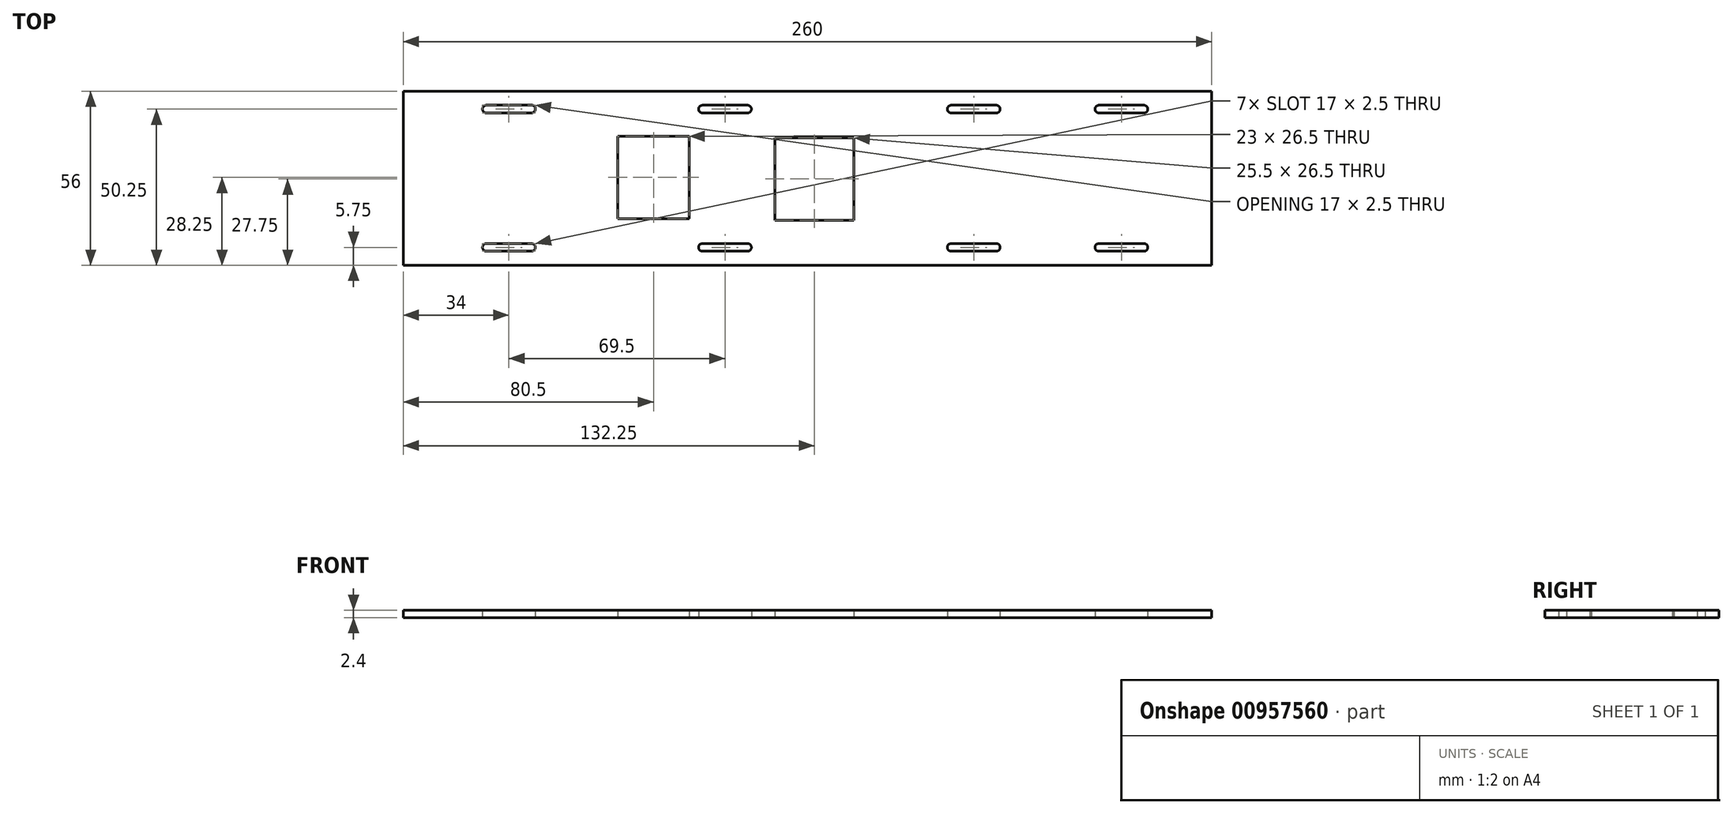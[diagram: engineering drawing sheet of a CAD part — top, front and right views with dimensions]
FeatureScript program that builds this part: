
annotation { "Feature Type Name" : "Feature", "Feature Type Description" : "" }
export const myFeature = defineFeature(function(context is Context, id is Id, definition is map)
    precondition{}
    {
        {
            var Q0;
            Q0=qCreatedBy(makeId("Top.planeOp"),FACE);
            var sketch = newSketch(context, id + "F0", { "sketchPlane" : qUnion([Q0])});
            skLineSegment(sketch, "E0.bottom", {"start": v(130, -28) * mm, "end": v(-130, -28) * mm});
            skLineSegment(sketch, "E0.top", {"start": v(130, 28) * mm, "end": v(-130, 28) * mm});
            skLineSegment(sketch, "E0.left", {"start": v(130, -28) * mm, "end": v(130, 28) * mm});
            skLineSegment(sketch, "E0.right", {"start": v(-130, -28) * mm, "end": v(-130, 28) * mm});
            skPoint(sketch, "E0.middle", {"position": v(0, 0) * mm});
            skLineSegment(sketch, "E1", {"start": v(-130, 28) * mm, "end": v(-104.5, 28) * mm});
            skLineSegment(sketch, "E2", {"start": v(-103.25, 23.5) * mm, "end": v(-88.5, 23.5) * mm});
            skLineSegment(sketch, "E3", {"start": v(-87.5, 22.5) * mm, "end": v(-87.5, 22.25) * mm});
            skLineSegment(sketch, "E4", {"start": v(-88.75, 21) * mm, "end": v(-103.25, 21) * mm});
            skLineSegment(sketch, "E5", {"start": v(-104.5, 22.25) * mm, "end": v(-104.5, 22.25) * mm});
            skLineSegment(sketch, "E6", {"start": v(-130, -28) * mm, "end": v(-104.5, -28) * mm});
            skLineSegment(sketch, "E7.bottom", {"start": v(-103.25, -23.5) * mm, "end": v(-88.75, -23.5) * mm});
            skLineSegment(sketch, "E7.top", {"start": v(-103.25, -21) * mm, "end": v(-88.75, -21) * mm});
            skLineSegment(sketch, "E7.left", {"start": v(-104.5, -22.25) * mm, "end": v(-104.5, -22.25) * mm});
            skLineSegment(sketch, "E7.right", {"start": v(-87.5, -22.25) * mm, "end": v(-87.5, -22.25) * mm});
            skLineSegment(sketch, "E8", {"start": v(-130, -28) * mm, "end": v(-35, -28) * mm});
            skLineSegment(sketch, "E9.bottom", {"start": v(-33.75, -23.5) * mm, "end": v(-19.25, -23.5) * mm});
            skLineSegment(sketch, "E9.top", {"start": v(-33.75, -21) * mm, "end": v(-19.25, -21) * mm});
            skLineSegment(sketch, "E9.left", {"start": v(-35, -22.25) * mm, "end": v(-35, -22.25) * mm});
            skLineSegment(sketch, "E9.right", {"start": v(-18, -22.25) * mm, "end": v(-18, -22.25) * mm});
            skLineSegment(sketch, "E10", {"start": v(-130, 28) * mm, "end": v(-35, 28) * mm});
            skLineSegment(sketch, "E11.bottom", {"start": v(-33.75, 23.5) * mm, "end": v(-19.25, 23.5) * mm});
            skLineSegment(sketch, "E11.top", {"start": v(-33.75, 21) * mm, "end": v(-19.25, 21) * mm});
            skLineSegment(sketch, "E11.left", {"start": v(-35, 22.25) * mm, "end": v(-35, 22.25) * mm});
            skLineSegment(sketch, "E11.right", {"start": v(-18, 22.25) * mm, "end": v(-18, 22.25) * mm});
            skLineSegment(sketch, "E12", {"start": v(130, 28) * mm, "end": v(109.5, 28) * mm});
            skLineSegment(sketch, "E13.bottom", {"start": v(108.25, 23.5) * mm, "end": v(93.75, 23.5) * mm});
            skLineSegment(sketch, "E13.top", {"start": v(108.25, 21) * mm, "end": v(93.75, 21) * mm});
            skLineSegment(sketch, "E13.left", {"start": v(109.5, 22.25) * mm, "end": v(109.5, 22.25) * mm});
            skLineSegment(sketch, "E13.right", {"start": v(92.5, 22.25) * mm, "end": v(92.5, 22.25) * mm});
            skLineSegment(sketch, "E14.bottom", {"start": v(60.75, 23.5) * mm, "end": v(46.25, 23.5) * mm});
            skLineSegment(sketch, "E14.top", {"start": v(60.75, 21) * mm, "end": v(46.25, 21) * mm});
            skLineSegment(sketch, "E14.left", {"start": v(62, 22.25) * mm, "end": v(62, 22.25) * mm});
            skLineSegment(sketch, "E14.right", {"start": v(45, 22.25) * mm, "end": v(45, 22.25) * mm});
            skLineSegment(sketch, "E15", {"start": v(130, -28) * mm, "end": v(109.5, -28) * mm});
            skLineSegment(sketch, "E16.bottom", {"start": v(108.25, -23.5) * mm, "end": v(93.75, -23.5) * mm});
            skLineSegment(sketch, "E16.top", {"start": v(108.25, -21) * mm, "end": v(93.75, -21) * mm});
            skLineSegment(sketch, "E16.left", {"start": v(109.5, -22.25) * mm, "end": v(109.5, -22.25) * mm});
            skLineSegment(sketch, "E16.right", {"start": v(92.5, -22.25) * mm, "end": v(92.5, -22.25) * mm});
            skLineSegment(sketch, "E17", {"start": v(130, -28) * mm, "end": v(62, -28) * mm});
            skLineSegment(sketch, "E18.bottom", {"start": v(60.75, -23.5) * mm, "end": v(46.25, -23.5) * mm});
            skLineSegment(sketch, "E18.top", {"start": v(60.75, -21) * mm, "end": v(46.25, -21) * mm});
            skLineSegment(sketch, "E18.left", {"start": v(62, -22.25) * mm, "end": v(62, -22.25) * mm});
            skLineSegment(sketch, "E18.right", {"start": v(45, -22.25) * mm, "end": v(45, -22.25) * mm});
            skLineSegment(sketch, "E19", {"start": v(-130, 28) * mm, "end": v(-61, 28) * mm});
            skLineSegment(sketch, "E20", {"start": v(-61, 28) * mm, "end": v(-61, 13.5) * mm});
            skLineSegment(sketch, "E21.bottom", {"start": v(-61, 13.5) * mm, "end": v(-38, 13.5) * mm});
            skLineSegment(sketch, "E21.top", {"start": v(-61, -13) * mm, "end": v(-38, -13) * mm});
            skLineSegment(sketch, "E21.left", {"start": v(-61, 13.5) * mm, "end": v(-61, -13) * mm});
            skLineSegment(sketch, "E21.right", {"start": v(-38, 13.5) * mm, "end": v(-38, -13) * mm});
            skLineSegment(sketch, "E22", {"start": v(-130, -28) * mm, "end": v(-10.5, -28) * mm});
            skLineSegment(sketch, "E23", {"start": v(-10.5, -28) * mm, "end": v(-10.5, -13.5) * mm});
            skLineSegment(sketch, "E24.bottom", {"start": v(-10.5, -13.5) * mm, "end": v(15, -13.5) * mm});
            skLineSegment(sketch, "E24.top", {"start": v(-10.5, 13) * mm, "end": v(15, 13) * mm});
            skLineSegment(sketch, "E24.left", {"start": v(-10.5, -13.5) * mm, "end": v(-10.5, 13) * mm});
            skLineSegment(sketch, "E24.right", {"start": v(15, -13.5) * mm, "end": v(15, 13) * mm});
            skPoint(sketch, "E25.visualSharp", {"position": v(-87.5, 23.5) * mm});
            skArc(sketch, "E25.filletArc", {"start": v(-87.5, 22.5) * mm, "mid": v(-87.8, 23.2) * mm, "end": v(-88.5, 23.5) * mm});
            skPoint(sketch, "E26.visualSharp", {"position": v(-87.5, 21) * mm});
            skArc(sketch, "E26.filletArc", {"start": v(-88.75, 21) * mm, "mid": v(-87.87, 21.37) * mm, "end": v(-87.5, 22.25) * mm});
            skPoint(sketch, "E27.visualSharp", {"position": v(-104.5, 23.5) * mm});
            skArc(sketch, "E27.filletArc", {"start": v(-103.25, 23.5) * mm, "mid": v(-104.13, 23.13) * mm, "end": v(-104.5, 22.25) * mm});
            skPoint(sketch, "E28.visualSharp", {"position": v(-104.5, 21) * mm});
            skArc(sketch, "E28.filletArc", {"start": v(-104.5, 22.25) * mm, "mid": v(-104.13, 21.37) * mm, "end": v(-103.25, 21) * mm});
            skPoint(sketch, "E29.visualSharp", {"position": v(-104.5, -21) * mm});
            skArc(sketch, "E29.filletArc", {"start": v(-103.25, -21) * mm, "mid": v(-104.13, -21.37) * mm, "end": v(-104.5, -22.25) * mm});
            skPoint(sketch, "E30.visualSharp", {"position": v(-104.5, -23.5) * mm});
            skArc(sketch, "E30.filletArc", {"start": v(-104.5, -22.25) * mm, "mid": v(-104.13, -23.13) * mm, "end": v(-103.25, -23.5) * mm});
            skPoint(sketch, "E31.visualSharp", {"position": v(-87.5, -21) * mm});
            skArc(sketch, "E31.filletArc", {"start": v(-87.5, -22.25) * mm, "mid": v(-87.87, -21.37) * mm, "end": v(-88.75, -21) * mm});
            skPoint(sketch, "E32.visualSharp", {"position": v(-87.5, -23.5) * mm});
            skArc(sketch, "E32.filletArc", {"start": v(-88.75, -23.5) * mm, "mid": v(-87.87, -23.13) * mm, "end": v(-87.5, -22.25) * mm});
            skPoint(sketch, "E33.visualSharp", {"position": v(-35, 23.5) * mm});
            skArc(sketch, "E33.filletArc", {"start": v(-33.75, 23.5) * mm, "mid": v(-34.63, 23.13) * mm, "end": v(-35, 22.25) * mm});
            skPoint(sketch, "E34.visualSharp", {"position": v(-35, 21) * mm});
            skArc(sketch, "E34.filletArc", {"start": v(-35, 22.25) * mm, "mid": v(-34.63, 21.37) * mm, "end": v(-33.75, 21) * mm});
            skPoint(sketch, "E35.visualSharp", {"position": v(-18, 23.5) * mm});
            skArc(sketch, "E35.filletArc", {"start": v(-18, 22.25) * mm, "mid": v(-18.37, 23.13) * mm, "end": v(-19.25, 23.5) * mm});
            skPoint(sketch, "E36.visualSharp", {"position": v(-18, 21) * mm});
            skArc(sketch, "E36.filletArc", {"start": v(-19.25, 21) * mm, "mid": v(-18.37, 21.37) * mm, "end": v(-18, 22.25) * mm});
            skPoint(sketch, "E37.visualSharp", {"position": v(-35, -21) * mm});
            skArc(sketch, "E37.filletArc", {"start": v(-33.75, -21) * mm, "mid": v(-34.63, -21.37) * mm, "end": v(-35, -22.25) * mm});
            skPoint(sketch, "E38.visualSharp", {"position": v(-35, -23.5) * mm});
            skArc(sketch, "E38.filletArc", {"start": v(-35, -22.25) * mm, "mid": v(-34.63, -23.13) * mm, "end": v(-33.75, -23.5) * mm});
            skPoint(sketch, "E39.visualSharp", {"position": v(-18, -21) * mm});
            skArc(sketch, "E39.filletArc", {"start": v(-18, -22.25) * mm, "mid": v(-18.37, -21.37) * mm, "end": v(-19.25, -21) * mm});
            skPoint(sketch, "E40.visualSharp", {"position": v(-18, -23.5) * mm});
            skArc(sketch, "E40.filletArc", {"start": v(-19.25, -23.5) * mm, "mid": v(-18.37, -23.13) * mm, "end": v(-18, -22.25) * mm});
            skPoint(sketch, "E41.visualSharp", {"position": v(45, 23.5) * mm});
            skArc(sketch, "E41.filletArc", {"start": v(46.25, 23.5) * mm, "mid": v(45.37, 23.13) * mm, "end": v(45, 22.25) * mm});
            skPoint(sketch, "E42.visualSharp", {"position": v(45, 21) * mm});
            skArc(sketch, "E42.filletArc", {"start": v(45, 22.25) * mm, "mid": v(45.37, 21.37) * mm, "end": v(46.25, 21) * mm});
            skPoint(sketch, "E43.visualSharp", {"position": v(62, 23.5) * mm});
            skArc(sketch, "E43.filletArc", {"start": v(62, 22.25) * mm, "mid": v(61.63, 23.13) * mm, "end": v(60.75, 23.5) * mm});
            skPoint(sketch, "E44.visualSharp", {"position": v(62, 21) * mm});
            skArc(sketch, "E44.filletArc", {"start": v(60.75, 21) * mm, "mid": v(61.63, 21.37) * mm, "end": v(62, 22.25) * mm});
            skPoint(sketch, "E45.visualSharp", {"position": v(45, -21) * mm});
            skArc(sketch, "E45.filletArc", {"start": v(46.25, -21) * mm, "mid": v(45.37, -21.37) * mm, "end": v(45, -22.25) * mm});
            skPoint(sketch, "E46.visualSharp", {"position": v(45, -23.5) * mm});
            skArc(sketch, "E46.filletArc", {"start": v(45, -22.25) * mm, "mid": v(45.37, -23.13) * mm, "end": v(46.25, -23.5) * mm});
            skPoint(sketch, "E47.visualSharp", {"position": v(62, -21) * mm});
            skArc(sketch, "E47.filletArc", {"start": v(62, -22.25) * mm, "mid": v(61.63, -21.37) * mm, "end": v(60.75, -21) * mm});
            skPoint(sketch, "E48.visualSharp", {"position": v(62, -23.5) * mm});
            skArc(sketch, "E48.filletArc", {"start": v(60.75, -23.5) * mm, "mid": v(61.63, -23.13) * mm, "end": v(62, -22.25) * mm});
            skPoint(sketch, "E49.visualSharp", {"position": v(92.5, 23.5) * mm});
            skArc(sketch, "E49.filletArc", {"start": v(93.75, 23.5) * mm, "mid": v(92.87, 23.13) * mm, "end": v(92.5, 22.25) * mm});
            skPoint(sketch, "E50.visualSharp", {"position": v(92.5, 21) * mm});
            skArc(sketch, "E50.filletArc", {"start": v(92.5, 22.25) * mm, "mid": v(92.87, 21.37) * mm, "end": v(93.75, 21) * mm});
            skPoint(sketch, "E51.visualSharp", {"position": v(109.5, 23.5) * mm});
            skArc(sketch, "E51.filletArc", {"start": v(109.5, 22.25) * mm, "mid": v(109.13, 23.13) * mm, "end": v(108.25, 23.5) * mm});
            skPoint(sketch, "E52.visualSharp", {"position": v(109.5, 21) * mm});
            skArc(sketch, "E52.filletArc", {"start": v(108.25, 21) * mm, "mid": v(109.13, 21.37) * mm, "end": v(109.5, 22.25) * mm});
            skPoint(sketch, "E53.visualSharp", {"position": v(92.5, -21) * mm});
            skArc(sketch, "E53.filletArc", {"start": v(93.75, -21) * mm, "mid": v(92.87, -21.37) * mm, "end": v(92.5, -22.25) * mm});
            skPoint(sketch, "E54.visualSharp", {"position": v(92.5, -23.5) * mm});
            skArc(sketch, "E54.filletArc", {"start": v(92.5, -22.25) * mm, "mid": v(92.87, -23.13) * mm, "end": v(93.75, -23.5) * mm});
            skPoint(sketch, "E55.visualSharp", {"position": v(109.5, -21) * mm});
            skArc(sketch, "E55.filletArc", {"start": v(109.5, -22.25) * mm, "mid": v(109.13, -21.37) * mm, "end": v(108.25, -21) * mm});
            skPoint(sketch, "E56.visualSharp", {"position": v(109.5, -23.5) * mm});
            skArc(sketch, "E56.filletArc", {"start": v(108.25, -23.5) * mm, "mid": v(109.13, -23.13) * mm, "end": v(109.5, -22.25) * mm});
            skSolve(sketch);
        }
        {
            var Q0;
            {var subQ1=sQuery(id+"F0.wireOp",EDGE,"E0.bottom");Q0=makeQuery(id+"F0.imprint","IMPRINT",FACE,{"disambiguationData":[TD([[makeQuery(id+"F0.imprint","IMPRINT",EDGE,{"derivedFrom":subQ1}),-1.0]])]});}
            extrude(context, id + "F1", {"entities" : qUnion([Q0]), "depth" : 2.4 * mm, "offsetDistance" : 25 * mm});
        }
    });
